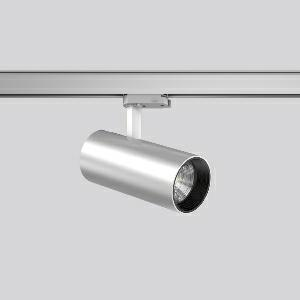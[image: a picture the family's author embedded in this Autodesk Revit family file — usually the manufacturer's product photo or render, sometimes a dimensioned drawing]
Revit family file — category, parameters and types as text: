
# Revit family: deecos_s_mini_742201_004_1_76_f828
name_source: partatom
category: Lighting Fixtures
units: mm (PartAtom-declared; Revit-internal decimal feet)

## family parameters
Cut with Voids When Loaded = No
Host = Face
Light Source = No
Part Type = Normal
Room Calculation Point = No
Round Connector Dimension = Use Diameter
Shared = No

## types (1)
- DEECOS S mini (1 x LED Modul 940, 2450 lm, 4000)
    Apparent Load = 20 VA
    Approval mark = CE
    CIE Flux Codes = 80 99 100 100 100
    Color Rendering = 92
    Color Temperature = 4000
    Default Elevation = 1800 mm
    Description = Series: DEECOS S mini
LED surface-mounted projector in modern design with no visible cooling ribs. Housing: die-cast aluminium, powder-coated. Rotation range: 356°. Swivel range: 90°. Black plastic ring and recessed LED to prevent glare from the side. Optical assembly with lens made of plastic (polycarbonate) for the best homogeneous light distribution - can be changed without tools. Best colour rendering index Ra>90. With adapter for RZB 3-circuit DALI tracks. Suitable for Track on ceiling, Wall track. High quality converter without flickering and stroboscopic effect. The following accessories can be mounted without use of tools: interchangeable lenses, decorative glasses, honeycomb louvre, clear and frosted diffusers, white interchangeable plastic ring. 
Colour: silver
Diameter: 87 mm
Height: 214 mm
Lamp: LED
Socket: without socket
Colour temperature: 4000K
Colour rendering index (CRI): 92
System power: 20 W
Rated luminous flux: 2450 lm
Luminous efficiency: 123 lm/W
Control gear: Converter, dimmable, DALI
Protection class: I
Type of protection: IP 20
    Height = 214 mm
    Lamp = 1 x LED Modul 940
    Lamp Light Flux = 2450 lm
    Lamp count = 1
    Length = 87 mm
    Lifetime = 50000 h
    Luminous efficacy = 123 lm/W
    Manufacturer = RZB
    ModVariant = No
    Model = 742201.004.1.76
    Mounting Place = Ceiling
    Mounting Type = Rail mounted
    Number of Poles = 1
    OnlyDefault = Yes
    Power Factor = 1
    Product Name = DEECOS S mini
    Product group = Track mounted projectors
    ProductGroupID = 301
    Protection Class = Protection class I
    Protection Degree = IP 20
    RLX_Detail_Level = 1
    RLX_Emergency_Light_Flux = 0 lm
    RLX_Emergency_Type = 0
    RLX_Emergency_Type_DB = No
    RlxData = <blob elided: 37569 chars, md5=ca5c2347>
    Socket = socket
    Standby Power = 0 W
    System Light Flux = 2450 lm
    System Power = 20 W
    Type Comments = Product without accessories
    Type Image = 741930.004.jpg
    URL = http://relux.com
    VarID = ---
    Voltage = 230 V
    Voltage Range = 220-240 V
    Weight = 0.00 kg
    Width = 0 mm  [stored 0 ft]

note: [stored X ft] marks values corroborated as IEEE doubles in the binary element streams (Revit-internal decimal feet)

## geometry (parser evidence)
native form markers: Blend x4, Sweep x13
no freeform markers — native parametric forms only
